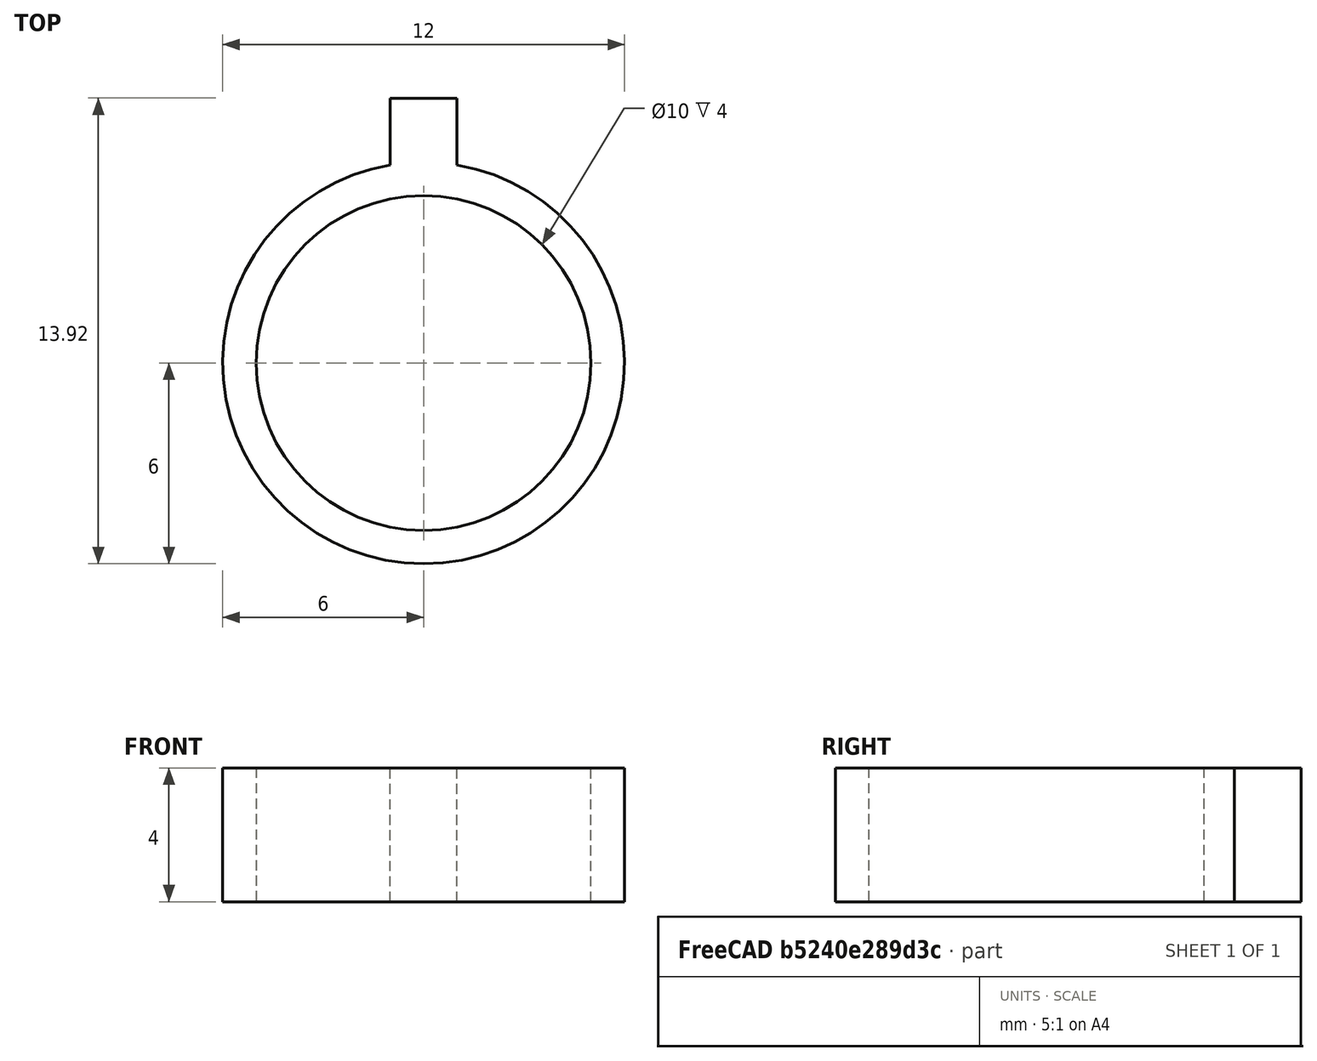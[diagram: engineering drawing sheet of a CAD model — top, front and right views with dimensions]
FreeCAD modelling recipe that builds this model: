
FCSTD DOCUMENT  (FreeCAD 0.20R29603 (Git))
Label: FingerRing_Connector
License: All rights reserved
LicenseURL: http://en.wikipedia.org/wiki/All_rights_reserved
objects: Sketcher::SketchObject×1, PartDesign::Pad×1, PartDesign::Body×1
note: 4 computed .brp shape members not serialized (recipe doc carries the construction recipe); baked Part::Feature solids carry a one-line shape summary decoded from their .brp

FEATURE [Sketcher::SketchObject] Sketch
  FullyConstrained = true
  MapMode = 5
  Support = -> [XY_Plane]
  sketch-geometry (5):
    g0: Circle CenterX=0 CenterY=0 CenterZ=0 NormalX=0 NormalY=0 NormalZ=1 AngleXU=0 Radius=5
    g1: ArcOfCircle CenterX=0 CenterY=0 CenterZ=0 NormalX=0 NormalY=0 NormalZ=1 AngleXU=0 Radius=6 StartAngle=1.73824 EndAngle=7.68653
    g2: LineSegment StartX=1 StartY=5.91608 StartZ=0 EndX=1 EndY=7.91608 EndZ=0
    g3: LineSegment StartX=1 StartY=7.91608 StartZ=0 EndX=-1 EndY=7.91608 EndZ=0
    g4: LineSegment StartX=-1 StartY=7.91608 StartZ=0 EndX=-1 EndY=5.91608 EndZ=0
  constraints (14):
    c: Coincident(g0,g-1)
    c: Coincident(g1,g0)
    c: Diameter(g0) = 10
    c: Diameter(g1) = 12
    c: Vertical(g2)
    c: Coincident(g2,g3)
    c: Coincident(g3,g4)
    c: Vertical(g4)
    c: Coincident(g1,g2)
    c: Coincident(g1,g4)
    c: Symmetric(g1,g1,g-2)
    c: Symmetric(g2,g3,g-2)
    c: DistanceX(g3,g3) = 2
    c: DistanceY(g2,g2) = 2
FEATURE [PartDesign::Pad] Pad
  Direction = (0,0,1)
  Length = 4
  Length2 = 10
  Profile = -> Sketch
  ReferenceAxis = -> Sketch [N_Axis]
  Type = 0
FEATURE [PartDesign::Body] Body
  Group = -> [Sketch,Pad]
  Origin = -> Origin
  Tip = -> Pad
